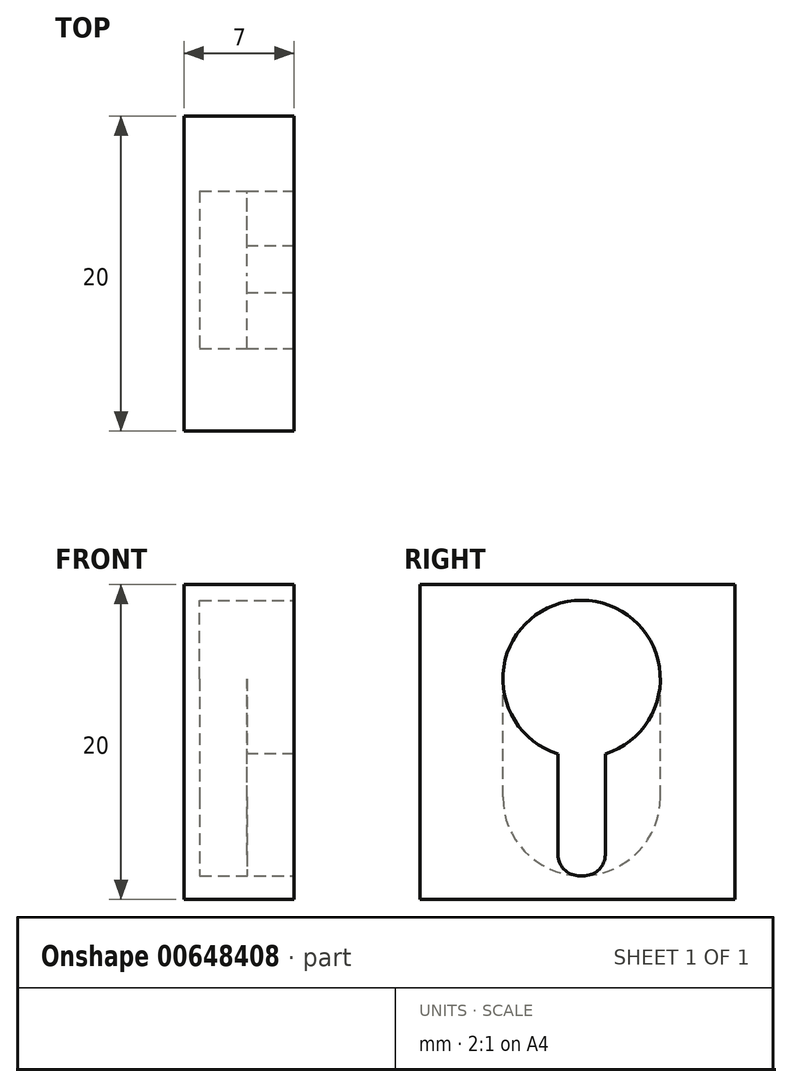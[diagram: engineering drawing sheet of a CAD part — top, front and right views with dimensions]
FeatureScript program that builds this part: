
annotation { "Feature Type Name" : "Feature", "Feature Type Description" : "" }
export const myFeature = defineFeature(function(context is Context, id is Id, definition is map)
    precondition{}
    {
        {
            var Q0;
            Q0=qCreatedBy(makeId("Top.planeOp"),FACE);
            var sketch = newSketch(context, id + "F0", { "sketchPlane" : qUnion([Q0])});
            skLineSegment(sketch, "E0.bottom", {"start": v(-3.42, 9.75) * mm, "end": v(-10.42, 9.75) * mm});
            skLineSegment(sketch, "E0.top", {"start": v(-3.42, -10.25) * mm, "end": v(-10.42, -10.25) * mm});
            skLineSegment(sketch, "E0.left", {"start": v(-3.42, 9.75) * mm, "end": v(-3.42, -10.25) * mm});
            skLineSegment(sketch, "E0.right", {"start": v(-10.42, 9.75) * mm, "end": v(-10.42, -10.25) * mm});
            skSolve(sketch);
        }
        {
            var Q0;
            Q0 = qSketchRegion(id + "F0", true);
            extrude(context, id + "F1", {"entities" : qUnion([Q0]), "depth" : 20 * mm, "offsetDistance" : 25 * mm});
        }
        {
            var Q0;
            Q0=makeQuery(id+"F1.opExtrude","SWEPT_FACE",FACE,{"disambiguationData":[OSD([sQuery(id+"F0.wireOp",EDGE,"E0.left")])]});
            var sketch = newSketch(context, id + "F2", { "sketchPlane" : qUnion([Q0])});
            skPoint(sketch, "E1.middle", {"position": v(-0.11, 9) * mm});
            skLineSegment(sketch, "E2", {"start": v(0, 0) * mm, "end": v(0, 9) * mm, "construction": true});
            skLineSegment(sketch, "E3", {"start": v(0, 20) * mm, "end": v(0, 19) * mm, "construction": true});
            skArc(sketch, "E4", {"start": v(5, 14) * mm, "mid": v(0, 19) * mm, "end": v(-5, 14) * mm});
            skLineSegment(sketch, "E5.left", {"start": v(5, 14) * mm, "end": v(5, 6.5) * mm});
            skLineSegment(sketch, "E5.right", {"start": v(-5, 14) * mm, "end": v(-5, 6.5) * mm});
            skPoint(sketch, "E5.middle", {"position": v(0, 9) * mm});
            skPoint(sketch, "E6.orphan", {"position": v(-5, 16.5) * mm});
            skPoint(sketch, "E7.orphan", {"position": v(5, 16.5) * mm});
            skLineSegment(sketch, "E8.trimOffspring", {"start": v(0, 14) * mm, "end": v(0, 20) * mm, "construction": true});
            skLineSegment(sketch, "E9", {"start": v(0, 9) * mm, "end": v(-0.11, 9) * mm, "construction": true});
            skArc(sketch, "E10", {"start": v(-5, 6.5) * mm, "mid": v(-3.54, 2.96) * mm, "end": v(0, 1.5) * mm});
            skArc(sketch, "E11.MirrorCS", {"start": v(5, 6.5) * mm, "mid": v(3.54, 2.96) * mm, "end": v(0, 1.5) * mm});
            skPoint(sketch, "E12.orphan", {"position": v(5, 1.5) * mm});
            skPoint(sketch, "E13.start.orphan", {"position": v(-5, 9) * mm});
            skPoint(sketch, "E14.orphan", {"position": v(-5, 1.5) * mm});
            skSolve(sketch);
        }
        {
            var Q0;
            Q0 = qSketchRegion(id + "F2", true);
            extrude(context, id + "F3", {"entities" : qUnion([Q0]), "operationType" : NewBodyOperationType.REMOVE, "oppositeDirection" : true, "depth" : 6 * mm, "offsetDistance" : 25 * mm});
        }
        {
            var Q0;
            Q0=makeQuery(id+"F2.imprint","IMPRINT",FACE,{"disambiguationData":[TD([[makeQuery(id+"F2.imprint","IMPRINT",EDGE,{"derivedFrom":sQuery(id+"F2.wireOp",EDGE,"E4")}),-1.0]])]});
            var sketch = newSketch(context, id + "F4", { "sketchPlane" : qUnion([Q0])});
            skLineSegment(sketch, "E15.bottom", {"start": v(-19.68, 0) * mm, "end": v(17.03, 0) * mm});
            skLineSegment(sketch, "E15.top", {"start": v(-19.68, 22.04) * mm, "end": v(17.03, 22.04) * mm});
            skLineSegment(sketch, "E15.left", {"start": v(-19.68, 0) * mm, "end": v(-19.68, 22.04) * mm});
            skLineSegment(sketch, "E15.right", {"start": v(17.03, 0) * mm, "end": v(17.03, 22.04) * mm});
            skSolve(sketch);
        }
        {
            var Q0;
            Q0 = qSketchRegion(id + "F4", true);
            extrude(context, id + "F5", {"entities" : qUnion([Q0]), "operationType" : NewBodyOperationType.REMOVE, "oppositeDirection" : true, "depth" : 3 * mm, "offsetDistance" : 25 * mm});
        }
        {
            var Q0;
            Q0=makeQuery(id+"F5.boolean.opBoolean","COPY",FACE,{"derivedFrom":makeQuery(id+"F5.opExtrude","CAP_FACE",FACE,{"disambiguationData":[OSD([sQuery(id+"F4.wireOp",EDGE,"E15.bottom"),sQuery(id+"F4.wireOp",EDGE,"E15.top"),sQuery(id+"F4.wireOp",EDGE,"E15.left"),sQuery(id+"F4.wireOp",EDGE,"E15.right")])],"isStart":false})});
            var sketch = newSketch(context, id + "F6", { "sketchPlane" : qUnion([Q0])});
            skLineSegment(sketch, "E16.bottom", {"start": v(-10.25, 20) * mm, "end": v(9.75, 20) * mm});
            skLineSegment(sketch, "E16.top", {"start": v(-10.25, 0) * mm, "end": v(9.75, 0) * mm});
            skLineSegment(sketch, "E16.left", {"start": v(-10.25, 20) * mm, "end": v(-10.25, 0) * mm});
            skLineSegment(sketch, "E16.right", {"start": v(9.75, 20) * mm, "end": v(9.75, 0) * mm});
            skLineSegment(sketch, "E17", {"start": v(0, 0) * mm, "end": v(0, 9) * mm, "construction": true});
            skPoint(sketch, "E17.endSnap0", {"position": v(0, 19) * mm});
            skArc(sketch, "E18", {"start": v(1.5, 9.23) * mm, "mid": v(0, 19) * mm, "end": v(-1.5, 9.23) * mm});
            skLineSegment(sketch, "E19.0", {"start": v(1.5, 2.84) * mm, "end": v(1.5, 9.23) * mm});
            skLineSegment(sketch, "E20.MirrorCS", {"start": v(-1.5, 2.84) * mm, "end": v(-1.5, 9.23) * mm});
            skPoint(sketch, "E21.trimOffspring.end.orphan", {"position": v(-1.5, 20) * mm});
            skPoint(sketch, "E22.trimOffspring.end.orphan", {"position": v(1.5, 20) * mm});
            skLineSegment(sketch, "E23.trimOffspring", {"start": v(0, 19) * mm, "end": v(0, 20) * mm, "construction": true});
            skArc(sketch, "E24", {"start": v(-0.22, 1.5) * mm, "mid": v(0, 1.5) * mm, "end": v(0.22, 1.5) * mm});
            skPoint(sketch, "E25.orphan", {"position": v(-1.5, 0) * mm});
            skPoint(sketch, "E26.orphan", {"position": v(1.5, 0) * mm});
            skPoint(sketch, "E27.visualSharp", {"position": v(-1.5, 1.73) * mm});
            skArc(sketch, "E27.filletArc", {"start": v(-1.5, 2.84) * mm, "mid": v(-1.13, 1.92) * mm, "end": v(-0.22, 1.5) * mm});
            skPoint(sketch, "E28.visualSharp", {"position": v(1.5, 1.73) * mm});
            skArc(sketch, "E28.filletArc", {"start": v(0.22, 1.5) * mm, "mid": v(1.13, 1.92) * mm, "end": v(1.5, 2.84) * mm});
            skSolve(sketch);
        }
        {
            var Q0;
            Q0 = qSketchRegion(id + "F6", true);
            extrude(context, id + "F7", {"entities" : qUnion([Q0]), "operationType" : NewBodyOperationType.ADD, "depth" : 3 * mm, "offsetDistance" : 25 * mm});
        }
    });
